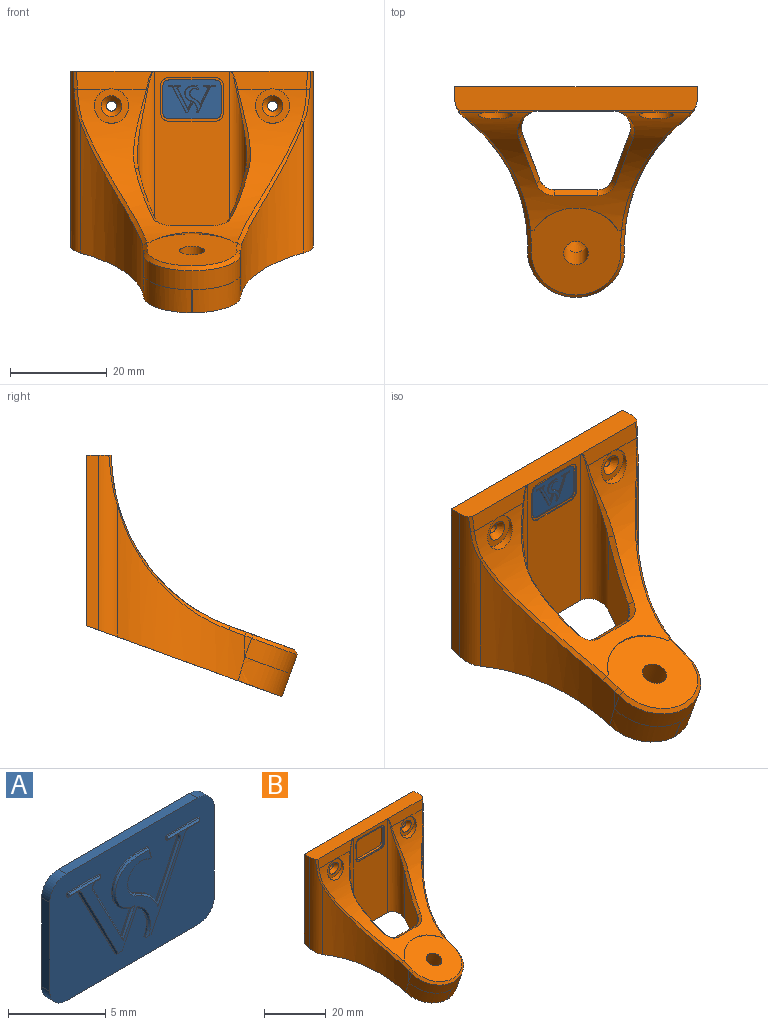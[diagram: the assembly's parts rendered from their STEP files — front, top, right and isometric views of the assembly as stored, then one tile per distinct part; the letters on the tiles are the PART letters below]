
ASSEMBLY  parts=2 mates=1
PART A: 71 faces, bbox 12x0.8x8 mm
  f0: plane 0.6x0.1mm, normal (0,0,-1), area 0.1mm2, adj f25,f27,f31,f59
  f1: plane 5.23x2.72mm, normal (-0.89,0,-0.46), area 0.6mm2, adj f2,f27,f31,f55
  f2: plane 0.41x0.1mm, normal (0,0,-1), area 0mm2, adj f1,f3,f31,f53
  f3: plane 2.23x1.07mm, normal (0.9,0,-0.43), area 0.2mm2, adj f2,f4,f31,f51
  f4: cylinder r=1.71mm len=2.23mm, axis (0,1,0), area 0.3mm2, adj f3,f5,f31,f49
  f5: plane 0.41x0.1mm, normal (0,0,-1), area 0mm2, adj f4,f6,f31,f47
  f6: plane 5.22x2.5mm, normal (0.9,0,-0.43), area 0.6mm2, adj f5,f28,f31,f45
  f7: plane 0.82x0.1mm, normal (0,0,-1), area 0.1mm2, adj f8,f28,f31,f41
  f8: plane 0.24x0.1mm, normal (1,0,0), area 0mm2, adj f7,f9,f31,f42
  f9: plane 2.4x0.1mm, normal (0,0,1), area 0.2mm2, adj f8,f10,f31,f44
  f10: plane 0.24x0.1mm, normal (-1,0,0), area 0mm2, adj f9,f11,f31,f46
  f11: plane 0.59x0.1mm, normal (0,0,-1), area 0.1mm2, adj f10,f29,f31,f48
  f12: plane 3.18x1.52mm, normal (-0.9,0,0.43), area 0.4mm2, adj f13,f29,f31,f52
  f13: cylinder r=2.42mm len=1.13mm, axis (0,1,0), area 0.2mm2, adj f12,f14,f31,f54
  f14: plane 0.45x0.21mm, normal (0.43,0,0.9), area 0mm2, adj f13,f15,f31,f56
  f15: cylinder r=0.96mm len=1.83mm, axis (0,1,0), area 0.3mm2, adj f14,f16,f31,f58
  f16: plane 0.24x0.1mm, normal (0,0,-1), area 0mm2, adj f15,f17,f31,f60
  f17: plane 0.77x0.21mm, normal (0.97,0,0.26), area 0.1mm2, adj f16,f18,f31,f62
  f18: plane 1x0.1mm, normal (0,0,1), area 0.1mm2, adj f17,f19,f31,f64
  f19: cylinder r=1.61mm len=3.19mm, axis (0,1,0), area 0.5mm2, adj f18,f20,f31,f66
  f20: plane 1.46x0.7mm, normal (-0.9,0,0.43), area 0.2mm2, adj f19,f21,f31,f68
  f21: plane 4.06x2.11mm, normal (0.89,0,0.46), area 0.5mm2, adj f20,f30,f31,f70
  f22: plane 0.35x0.1mm, normal (0,0,-1), area 0mm2, adj f23,f30,f31,f67
  f23: plane 0.24x0.1mm, normal (1,0,0), area 0mm2, adj f22,f24,f31,f65
  f24: plane 2.4x0.1mm, normal (0,0,1), area 0.2mm2, adj f23,f25,f31,f63
  f25: plane 0.24x0.1mm, normal (-1,0,0), area 0mm2, adj f0,f24,f31,f61
  f26: plane 9.4x5.4mm, normal (0,-1,0), area 10.1mm2, adj f41,f42,f43,f44,f45,f46,f47,f48
  f27: cylinder r=0.24mm len=0.21mm, axis (0,1,0), area 0mm2, adj f0,f1,f31,f57
  f28: cylinder r=0.24mm len=0.22mm, axis (0,-1,0), area 0mm2, adj f6,f7,f31,f43
  f29: cylinder r=0.24mm len=0.34mm, axis (0,-1,0), area 0mm2, adj f11,f12,f31,f50
  f30: cylinder r=0.24mm len=0.35mm, axis (0,1,0), area 0mm2, adj f21,f22,f31,f69
  f31: plane 12x8mm, normal (0,-1,0), area 79.8mm2, adj f0,f1,f2,f3,f4,f5,f6,f7
  f32: plane 5.6x0.6mm, normal (1,0,0), area 3.4mm2, adj f31,f33,f39,f40
  f33: cylinder r=1.2mm len=1.2mm, axis (0,-1,0), area 1.1mm2, adj f31,f32,f34,f40
  f34: plane 9.6x0.6mm, normal (0,0,1), area 5.8mm2, adj f31,f33,f35,f40
  f35: cylinder r=1.2mm len=1.2mm, axis (0,-1,0), area 1.1mm2, adj f31,f34,f36,f40
  f36: plane 5.6x0.6mm, normal (-1,0,0), area 3.4mm2, adj f31,f35,f37,f40
  f37: cylinder r=1.2mm len=1.2mm, axis (0,-1,0), area 1.1mm2, adj f31,f36,f38,f40
  f38: plane 9.6x0.6mm, normal (0,0,-1), area 5.8mm2, adj f31,f37,f39,f40
  f39: cylinder r=1.2mm len=1.2mm, axis (0,-1,0), area 1.1mm2, adj f31,f32,f38,f40
  f40: plane 12x8mm, normal (0,1,0), area 94.8mm2, adj f32,f33,f34,f35,f36,f37,f38,f39
  f41: plane 0.82x0.1mm, normal (0,-0.71,-0.71), area 0.1mm2, adj f7,f26,f42,f43
  f42: plane 0.24x0.1mm, normal (0.71,-0.71,0), area 0mm2, adj f8,f26,f41,f44
  f43: cone r=0.34mm half-angle=45deg, axis (0,-1,0), area 0mm2, adj f26,f28,f41,f45
  f44: plane 2.4x0.1mm, normal (0,-0.71,0.71), area 0.3mm2, adj f9,f26,f42,f46
  f45: plane 5.27x2.56mm, normal (0.64,-0.71,-0.31), area 0.8mm2, adj f6,f26,f43,f47
  f46: plane 0.24x0.1mm, normal (-0.71,-0.71,0), area 0mm2, adj f10,f26,f44,f48
  f47: plane 0.41x0.1mm, normal (0,-0.71,-0.71), area 0mm2, adj f5,f26,f45,f49
  f48: plane 0.59x0.1mm, normal (0,-0.71,-0.71), area 0.1mm2, adj f11,f26,f46,f50
  f49: cone r=1.71mm half-angle=45deg, axis (0,-1,0), area 0.4mm2, adj f4,f26,f47,f51
  f50: cone r=0.34mm half-angle=45deg, axis (0,-1,0), area 0.1mm2, adj f26,f29,f48,f52
  f51: plane 2.37x1.13mm, normal (0.64,-0.71,-0.31), area 0.4mm2, adj f3,f26,f49,f53
  f52: plane 3.43x1.62mm, normal (-0.64,-0.71,0.31), area 0.5mm2, adj f12,f26,f50,f54
  f53: plane 0.41x0.1mm, normal (0,-0.71,-0.71), area 0mm2, adj f2,f26,f51,f55
  f54: cone r=2.32mm half-angle=45deg, axis (0,1,0), area 0.2mm2, adj f13,f26,f52,f56
  f55: plane 5.28x2.78mm, normal (-0.63,-0.71,-0.33), area 0.8mm2, adj f1,f26,f53,f57
  f56: plane 0.49x0.3mm, normal (0.31,-0.71,0.64), area 0.1mm2, adj f14,f26,f54,f58
  f57: cone r=0.34mm half-angle=45deg, axis (0,-1,0), area 0mm2, adj f26,f27,f55,f59
  f58: cone r=0.96mm half-angle=45deg, axis (0,-1,0), area 0.5mm2, adj f15,f26,f56,f60
  f59: plane 0.6x0.1mm, normal (0,-0.71,-0.71), area 0.1mm2, adj f0,f26,f57,f61
  f60: plane 0.24x0.1mm, normal (0,-0.71,-0.71), area 0mm2, adj f16,f26,f58,f62
  f61: plane 0.24x0.1mm, normal (-0.71,-0.71,0), area 0mm2, adj f25,f26,f59,f63
  f62: plane 0.77x0.28mm, normal (0.68,-0.71,0.18), area 0.1mm2, adj f17,f26,f60,f64
  f63: plane 2.4x0.1mm, normal (0,-0.71,0.71), area 0.3mm2, adj f24,f26,f61,f65
  f64: plane 1x0.1mm, normal (0,-0.71,0.71), area 0.1mm2, adj f18,f26,f62,f66
  f65: plane 0.24x0.1mm, normal (0.71,-0.71,0), area 0mm2, adj f23,f26,f63,f67
  f66: cone r=1.51mm half-angle=45deg, axis (0,1,0), area 0.7mm2, adj f19,f26,f64,f68
  f67: plane 0.35x0.1mm, normal (0,-0.71,-0.71), area 0mm2, adj f22,f26,f65,f69
  f68: plane 1.77x0.85mm, normal (-0.64,-0.71,0.31), area 0.3mm2, adj f20,f26,f66,f70
  f69: cone r=0.34mm half-angle=45deg, axis (0,-1,0), area 0.1mm2, adj f26,f30,f67,f70
  f70: plane 4.29x2.21mm, normal (0.63,-0.71,0.33), area 0.7mm2, adj f21,f26,f68,f69
PART B: 76 faces, bbox 51.1x50.5x66.8 mm
  f0: cylinder r=37.05mm len=47.25mm, axis (-1,0,0), area 524.7mm2, adj f1,f58,f59,f60,f61,f62,f65,f66
  f1: cylinder r=3.56mm len=7.11mm, axis (0,1,0), area 19.8mm2, adj f0,f2,f58
  f2: plane 7.11x7.11mm, normal (0,-1,0), area 25.5mm2, adj f1,f3
  f3: cone r=1.03mm half-angle=41deg, axis (0,-1,0), area 16.7mm2, adj f2,f4
  f4: cylinder r=1.03mm len=3.73mm, axis (0,-1,0), area 24.1mm2, adj f3,f5
  f5: plane 50x35.16mm, normal (0,1,0), area 1751.1mm2, adj f4,f6,f52,f53,f54,f55
  f6: plane 51.08x41.31mm, normal (0,0.34,-0.94), area 909.5mm2, adj f5,f7,f8,f9,f10,f11,f12,f14
  f7: plane 21.89x9.5mm, normal (-0.94,0.35,0), area 144.8mm2, adj f6,f8,f34,f70
  f8: cylinder r=3.14mm len=12.18mm, axis (0,0,1), area 41.5mm2, adj f6,f7,f9,f71
  f9: plane 10.43x9.02mm, normal (0,1,0), area 94.1mm2, adj f6,f8,f10,f72
  f10: cylinder r=3.14mm len=12.18mm, axis (0,0,1), area 41.5mm2, adj f6,f9,f11,f73
  f11: plane 21.89x9.5mm, normal (0.94,0.35,0), area 144.8mm2, adj f6,f10,f12,f74
  f12: cylinder r=3.46mm len=38.65mm, axis (0,0,1), area 186.7mm2, adj f6,f11,f13,f14,f75
  f13: bspline ~3.92x1.83mm, area 0.9mm2, adj f12,f14,f53,f58,f75
  f14: plane 37.01x15.63mm, normal (0,-1,0), area 462.1mm2, adj f6,f12,f13,f15,f16,f27,f28,f29
  f15: bspline ~3.92x1.83mm, area 0.9mm2, adj f14,f34,f53,f68,f69
  f16: cylinder r=1.7mm len=1.7mm, axis (0,-1,0), area 0.5mm2, adj f14,f17,f27,f33
  f17: plane 13x9mm, normal (0,-1,0), area 19.8mm2, adj f16,f18,f20,f21,f22,f23,f24,f25
  f18: plane 5.6x0.8mm, normal (1,0,0), area 4.5mm2, adj f17,f19,f20,f26
  f19: plane 12x8mm, normal (0,-1,0), area 94.8mm2, adj f18,f20,f21,f22,f23,f24,f25,f26
  f20: cylinder r=1.2mm len=1.2mm, axis (0,-1,0), area 1.5mm2, adj f17,f18,f19,f21
  f21: plane 9.6x0.8mm, normal (0,0,1), area 7.7mm2, adj f17,f19,f20,f22
  f22: cylinder r=1.2mm len=1.2mm, axis (0,-1,0), area 1.5mm2, adj f17,f19,f21,f23
  f23: plane 5.6x0.8mm, normal (-1,0,0), area 4.5mm2, adj f17,f19,f22,f24
  f24: cylinder r=1.2mm len=1.2mm, axis (0,-1,0), area 1.5mm2, adj f17,f19,f23,f25
  f25: plane 9.6x0.8mm, normal (0,0,-1), area 7.7mm2, adj f17,f19,f24,f26
  f26: cylinder r=1.2mm len=1.2mm, axis (0,-1,0), area 1.5mm2, adj f17,f18,f19,f25
  f27: plane 5.6x0.2mm, normal (1,0,0), area 1.1mm2, adj f14,f16,f17,f28
  f28: cylinder r=1.7mm len=1.7mm, axis (0,-1,0), area 0.5mm2, adj f14,f17,f27,f29
  f29: plane 9.6x0.2mm, normal (0,0,1), area 1.9mm2, adj f14,f17,f28,f30
  f30: cylinder r=1.7mm len=1.7mm, axis (0,-1,0), area 0.5mm2, adj f14,f17,f29,f31
  f31: plane 5.6x0.2mm, normal (-1,0,0), area 1.1mm2, adj f14,f17,f30,f32
  f32: cylinder r=1.7mm len=1.7mm, axis (0,-1,0), area 0.5mm2, adj f14,f17,f31,f33
  f33: plane 9.6x0.2mm, normal (0,0,-1), area 1.9mm2, adj f14,f16,f17,f32
  f34: cylinder r=3.46mm len=38.65mm, axis (0,0,1), area 186.7mm2, adj f6,f7,f14,f15,f69
  f35: cylinder r=5mm len=37.48mm, axis (0,0,1), area 154.8mm2, adj f6,f36,f37,f53,f54,f59
  f36: bspline ~4.02x0.91mm, area 3.1mm2, adj f35,f53,f58,f59
  f37: cylinder r=32.83mm len=35.97mm, axis (0,0,1), area 440.2mm2, adj f6,f35,f38,f45,f46,f60
  f38: plane 4.42x1.42mm, normal (-1,0,0), area 3.1mm2, adj f37,f39,f44
  f39: plane 1.69x1.27mm, normal (-0.71,-0.24,0.66), area 1.7mm2, adj f38,f40,f45,f62
  f40: cone r=9.2mm half-angle=45deg, axis (0,0.34,-0.94), area 34.1mm2, adj f39,f41,f44,f62
  f41: plane 1.69x1.27mm, normal (0.71,-0.24,0.66), area 1.7mm2, adj f40,f42,f43,f62
  f42: plane 4.42x1.42mm, normal (1,0,0), area 3.1mm2, adj f41,f44,f49
  f43: bspline ~3.47x1.94mm, area 3.9mm2, adj f41,f49,f62,f65
  f44: cylinder r=10mm len=20mm, axis (0,-0.34,0.94), area 130.4mm2, adj f38,f40,f42,f46,f48
  f45: bspline ~3.47x1.94mm, area 3.9mm2, adj f37,f39,f60,f62
  f46: bspline ~10.76x10.03mm, area 78.4mm2, adj f6,f37,f44,f47
  f47: plane 4.74x1.73mm, normal (0,-0.94,-0.34), area 0.1mm2, adj f6,f46,f48
  f48: bspline ~44.32x22.54mm, area 78.4mm2, adj f6,f44,f47,f49
  f49: cylinder r=32.83mm len=35.97mm, axis (0,0,1), area 440.2mm2, adj f6,f42,f43,f48,f50,f65
  f50: cylinder r=5mm len=37.48mm, axis (0,0,1), area 154.8mm2, adj f6,f49,f51,f52,f53,f66
  f51: bspline ~4.02x0.91mm, area 3.1mm2, adj f50,f53,f66,f68
  f52: plane 36.03x2.4mm, normal (1,0,0), area 85.5mm2, adj f5,f6,f50,f53
  f53: plane 50.07x5.07mm, normal (0,0,1), area 248.6mm2, adj f5,f13,f14,f15,f35,f36,f50,f51
  f54: plane 36.03x2.4mm, normal (-1,0,0), area 85.5mm2, adj f5,f6,f35,f53
  f55: cylinder r=1.03mm len=3.73mm, axis (0,-1,0), area 24.1mm2, adj f5,f56
  f56: cone r=1.03mm half-angle=41deg, axis (0,-1,0), area 16.7mm2, adj f55,f57
  f57: plane 7.11x7.11mm, normal (0,-1,0), area 25.5mm2, adj f56,f67
  f58: plane 15.85x3.7mm, normal (0,-1,0.09), area 54.7mm2, adj f0,f1,f13,f36,f53
  f59: bspline ~6.86x1.78mm, area 4.9mm2, adj f0,f35,f36,f60
  f60: bspline ~25.69x23.17mm, area 32.4mm2, adj f0,f37,f45,f59
  f61: cylinder r=10mm len=17.32mm, axis (0,0.34,-0.94), area 0mm2, adj f0,f62
  f62: plane 18.72x18.04mm, normal (0,-0.34,0.94), area 266.3mm2, adj f0,f39,f40,f41,f43,f45,f61,f63
  f63: cylinder r=2.55mm len=8.79mm, axis (0,-0.34,0.94), area 120.3mm2, adj f62,f64
  f64: cone r=0mm half-angle=59deg, axis (0,-0.34,0.94), area 23.9mm2, adj f63
  f65: bspline ~25.69x23.17mm, area 32.5mm2, adj f0,f43,f49,f66
  f66: bspline ~6.86x1.78mm, area 4.9mm2, adj f0,f50,f51,f65
  f67: cylinder r=3.56mm len=7.11mm, axis (0,1,0), area 19.8mm2, adj f0,f57,f68
  f68: plane 15.85x3.7mm, normal (0,-1,0.09), area 54.7mm2, adj f0,f15,f51,f53,f67
  f69: bspline ~16.57x5.39mm, area 14mm2, adj f0,f15,f34,f70
  f70: bspline ~10.85x10.25mm, area 18.4mm2, adj f0,f7,f69,f71
  f71: bspline ~3.68x3.26mm, area 6.3mm2, adj f0,f8,f70,f72
  f72: plane 9.02x1.23mm, normal (0,0.48,0.88), area 12.6mm2, adj f0,f9,f71,f73
  f73: bspline ~3.68x3.26mm, area 6.3mm2, adj f0,f10,f72,f74
  f74: bspline ~10.85x10.25mm, area 18.4mm2, adj f0,f11,f73,f75
  f75: bspline ~16.57x5.39mm, area 14mm2, adj f0,f12,f13,f74
PLACE A t=(0,-4.6,11.82)mm
PLACE B t=(0,-5,-10.68)mm
MATE fastened A.f40 <-> B.f19  axis (0,1,0) through (0,-4,11.82)mm
